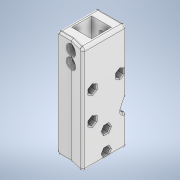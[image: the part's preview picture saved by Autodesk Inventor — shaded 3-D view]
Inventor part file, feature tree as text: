
AUTODESK INVENTOR PART (.ipt)
format: ipt  version: 2021 (Build 250183000, 183)  size: 570,880 bytes
history: native  units: mm
features: extrude x13, sketch x13, chamfer x5, fillet x4
ambient origin geometry x8: Origin, YZ Plane, XZ Plane, XY Plane, X Axis, Y Axis, Z Axis, Center Point
bodies: Solid1 (feature_tree)
feature tree (35):
  extrude  "Extrusion1"  Depth=15.0mm
  extrude  "Extrusion2"  Depth=110.0mm TaperAngle=0.0deg
  chamfer  "Chamfer1"  Distance=10.0mm
  extrude  "Extrusion3"  Depth=55.0mm
  extrude  "Extrusion7"  Depth=10.0mm
  fillet  "Fillet7"  Radius=14.0mm
  fillet  "Fillet8"  [1 undecoded]
  fillet  "Fillet9"  Radius=10.0mm
  extrude  "Extrusion8"  Depth=3.0mm
  extrude  "Extrusion9"  Depth=3.0mm
  chamfer  "Chamfer3"  Distance=30.0mm
  extrude  "Extrusion10"  Depth=55.0mm
  extrude  "Extrusion11"  Depth=10.0mm TaperAngle=0.0deg
  chamfer  "Chamfer4"  Distance=2.0mm Angle=45.0deg
  extrude  "Extrusion12"  Depth=10.0mm
  fillet  "Fillet10"  Radius=4.3mm
  extrude  "Extrusion13"  Depth=10.0mm
  chamfer  "Chamfer5"  Distance=4.3mm
  extrude  "Extrusion14"  Depth=10.0mm
  extrude  "Extrusion15"  Depth=10.0mm
  extrude  "Extrusion16"  Depth=10.0mm
  chamfer  "Chamfer6"  Distance=20.0mm
  sketch  "Sketch1"  dims[d0=43.5mm d1=15.0mm]
  sketch  "Sketch2"  dims[d2=36.0mm d3=110.0mm d4=0.0mm]
  sketch  "Sketch3"  dims[d7=3.0mm]
  sketch  "Sketch10"  dims[d8=8.0mm]
  sketch  "Sketch11"  dims[d9=5.5mm d10=10.0mm d11=0.0mm]
  sketch  "Sketch12"  dims[d12=1.0mm d13=2.0mm d14=45.0deg d15=55.0mm]
  sketch  "Sketch14"  dims[d16=4.363323mm d17=62.0mm d18=14.0mm d19=90.0deg d20=10.0mm d21=0.0mm]
  sketch  "Sketch15"  dims[d62=15.0mm d63=0.0mm d64=3.0mm]
  sketch  "Sketch16"  dims[d65=2.0mm d66=3.0mm]
  sketch  "Sketch17"  dims[d67=20.4mm]
  sketch  "Sketch18"  dims[d68=20.4mm d71=30.0mm d72=0.0mm]
  sketch  "Sketch19"  dims[d73=14.0mm d74=55.0mm]
  sketch  "Sketch20"  dims[d75=21.5mm d76=15.0mm d77=0.0mm d78=2.0mm d79=2.0mm d80=45.0deg d91=4.3mm d92=4.3mm d93=4.3mm d94=4.3mm d95=20.0mm d96=20.0mm d97=20.0mm d98=20.0mm d99=0.0mm d100=0.0mm d101=4.3mm d102=20.0mm d103=20.0mm d104=4.3mm d105=20.0mm d106=7.4mm d107=7.4mm d108=7.4mm d109=7.4mm d110=7.4mm d111=15.0mm d112=0.0mm d113=1.0mm d114=2.0mm d115=45.0deg d116=0.75mm d117=0.75mm d118=5.0mm d119=0.75mm d120=2.0mm d121=10.0mm d122=0.0mm d123=2.0mm d124=2.0mm d125=5.0mm d126=2.0mm d127=0.0mm d128=1.66666mm d129=2.0mm d130=45.0deg d131=4.8mm d132=11.175mm d133=4.3mm d134=10.2mm d135=4.3mm d136=10.2mm d137=8.0mm d138=12.0mm d139=45.0mm d140=0.0mm d141=10.0mm d142=10.0mm d143=5.5mm d144=0.0mm d145=2.0mm d146=5.5mm d147=0.0mm d148=0.0mm d149=0.5mm d150=2.0mm d151=45.0deg]
note: 1 required parameter value undecoded (feature->parameter linkage not recoverable at this tier; creation-order binding heuristic only, values carry confidence <= 0.55)
